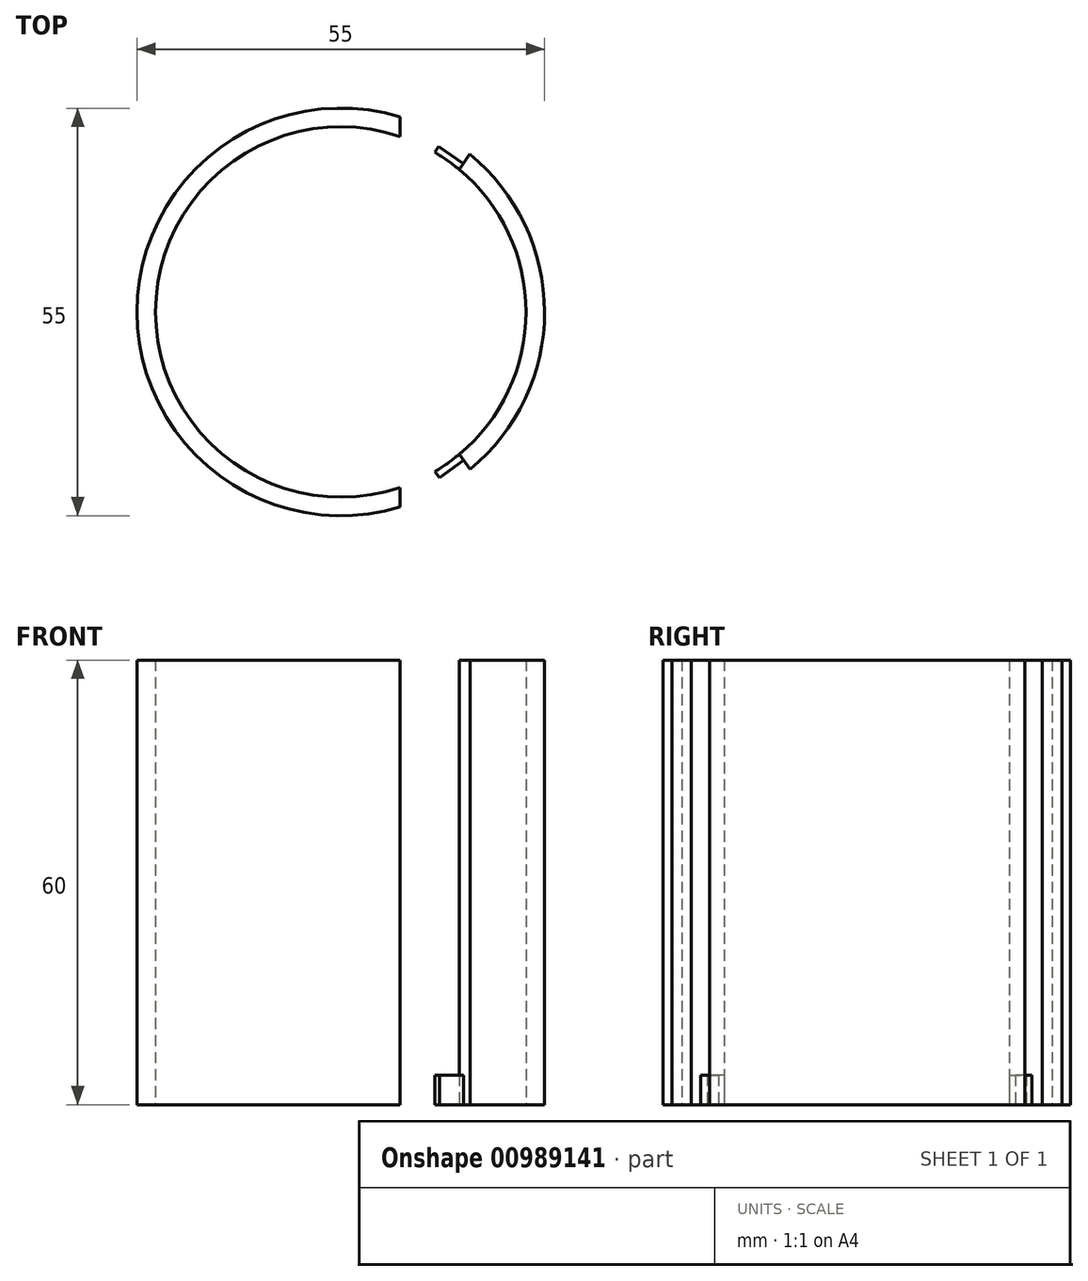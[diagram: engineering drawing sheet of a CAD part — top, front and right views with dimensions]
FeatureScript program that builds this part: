
annotation { "Feature Type Name" : "Feature", "Feature Type Description" : "" }
export const myFeature = defineFeature(function(context is Context, id is Id, definition is map)
    precondition{}
    {
        {
            var Q0;
            Q0=qCreatedBy(makeId("Top.planeOp"),FACE);
            var sketch = newSketch(context, id + "F0", { "sketchPlane" : qUnion([Q0])});
            skCircle(sketch, "E0", {"center": v(0, 0) * mm, "radius": 25 * mm});
            skCircle(sketch, "E1", {"center": v(0, 0) * mm, "radius": 27.5 * mm});
            skLineSegment(sketch, "E2", {"start": v(8, 26.31) * mm, "end": v(8, -26.31) * mm});
            skLineSegment(sketch, "E3", {"start": v(12.7, 21.53) * mm, "end": v(14.1, 23.6) * mm});
            skLineSegment(sketch, "E4", {"start": v(15.97, 19.23) * mm, "end": v(17.38, 21.31) * mm});
            skLineSegment(sketch, "E5", {"start": v(12.7, 21.53) * mm, "end": v(12.7, -21.53) * mm});
            skLineSegment(sketch, "E6", {"start": v(15.97, -19.23) * mm, "end": v(17.45, -21.25) * mm});
            skLineSegment(sketch, "E7", {"start": v(12.7, -21.53) * mm, "end": v(14.19, -23.56) * mm});
            skLineSegment(sketch, "E8", {"start": v(13.22, 22.3) * mm, "end": v(16.53, 20.06) * mm});
            skLineSegment(sketch, "E9", {"start": v(16.56, -20.04) * mm, "end": v(13.34, -22.4) * mm});
            skSolve(sketch);
        }
        {
            var Q0;
            {var subQ4=sQuery(id+"F0.wireOp",EDGE,"E2");var subQ5=sQuery(id+"F0.wireOp",EDGE,"E1");var subQ6=makeQuery(id+"F0.imprint","INTERSECT",VERTEX,{"disambiguationData":[OD(0.0)],"derivedFrom":[subQ5,subQ4]});Q0=makeQuery(id+"F0.imprint","IMPRINT",FACE,{"disambiguationData":[TD([[makeQuery(id+"F0.imprint","IMPRINT",EDGE,{"disambiguationData":[TD([[subQ6,1.0]])],"derivedFrom":subQ5}),1.0]])]});}
            var Q1;
            {var subQ0=sQuery(id+"F0.wireOp",EDGE,"E4");var subQ4=sQuery(id+"F0.wireOp",EDGE,"E0");var subQ5=makeQuery(id+"F0.imprint","INTERSECT",VERTEX,{"derivedFrom":[subQ4,subQ0]});Q1=makeQuery(id+"F0.imprint","IMPRINT",FACE,{"disambiguationData":[TD([[makeQuery(id+"F0.imprint","IMPRINT",EDGE,{"disambiguationData":[TD([[subQ5,1.0]])],"derivedFrom":subQ4}),-1.0]])]});}
            var Q2;
            {var subQ4=sQuery(id+"F0.wireOp",EDGE,"E2");var subQ5=sQuery(id+"F0.wireOp",EDGE,"E1");var subQ6=makeQuery(id+"F0.imprint","INTERSECT",VERTEX,{"disambiguationData":[OD(1.0)],"derivedFrom":[subQ5,subQ4]});Q2=makeQuery(id+"F0.imprint","IMPRINT",FACE,{"disambiguationData":[TD([[makeQuery(id+"F0.imprint","IMPRINT",EDGE,{"disambiguationData":[TD([[subQ6,-1.0]])],"derivedFrom":subQ5}),1.0]])]});}
            extrude(context, id + "F1", {"entities" : qUnion([Q0, Q1, Q2]), "depth" : 60 * mm, "offsetDistance" : 25.4 * mm});
        }
        {
            var Q0;
            {var subQ5=sQuery(id+"F0.wireOp",EDGE,"E9");Q0=makeQuery(id+"F0.imprint","IMPRINT",FACE,{"disambiguationData":[TD([[makeQuery(id+"F0.imprint","IMPRINT",EDGE,{"derivedFrom":subQ5}),-1.0]])]});}
            var Q1;
            {var subQ5=sQuery(id+"F0.wireOp",EDGE,"E8");Q1=makeQuery(id+"F0.imprint","IMPRINT",FACE,{"disambiguationData":[TD([[makeQuery(id+"F0.imprint","IMPRINT",EDGE,{"derivedFrom":subQ5}),-1.0]])]});}
            extrude(context, id + "F2", {"entities" : qUnion([Q0, Q1]), "depth" : 4 * mm, "offsetDistance" : 25.4 * mm});
        }
    });
